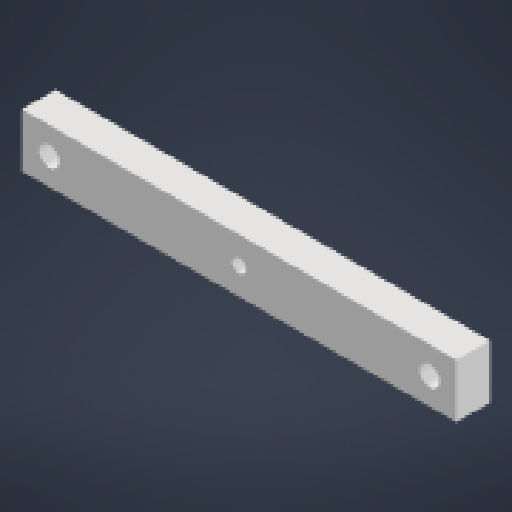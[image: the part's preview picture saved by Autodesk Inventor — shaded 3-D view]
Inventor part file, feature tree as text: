
AUTODESK INVENTOR PART (.ipt)
format: ipt  version: 2023.2 (Build 272271000, 271)  size: 136,704 bytes
history: native  units: mm
features: sketch x4, extrude x3, other x3, reference x2, projected_geometry x1
ambient origin geometry x8: Origin, YZ Plane, XZ Plane, XY Plane, X Axis, Y Axis, Z Axis, Center Point
bodies: Solid1 (feature_tree)
feature tree (13):
  extrude  "Extrusion1"  Depth=5.0mm
  sketch  "Sketch2"  dims[d4=32.297mm d5=1.8mm d6=0.0mm]
  extrude  "Extrusion2"  Depth=1.8mm TaperAngle=0.0deg
  extrude  "Extrusion3"  TaperAngle=0.0deg  [1 undecoded]
  sketch  "Sketch1"  dims[d0=5.0mm d1=0.0mm d2=3.9mm]
  reference  "Reference1"
  reference  "Reference2"
  sketch  "Sketch3"  dims[d7=2.0mm d8=0.0mm d9=0.0mm]
  projected_geometry  "Projected Loop1"
  sketch  "Sketch4"
  parser-record x1  (decoder bookkeeping rows leaked as tree rows — omitted from the tree; the rows remain in map.json)
  other  "turret_assembly.iam"
  other  "upper_grip:1"
note: 1 required parameter value undecoded (feature->parameter linkage not recoverable at this tier; creation-order binding heuristic only, values carry confidence <= 0.55)
note: 1 file-system path scrubbed to <path> (originals preserved in map.json)
